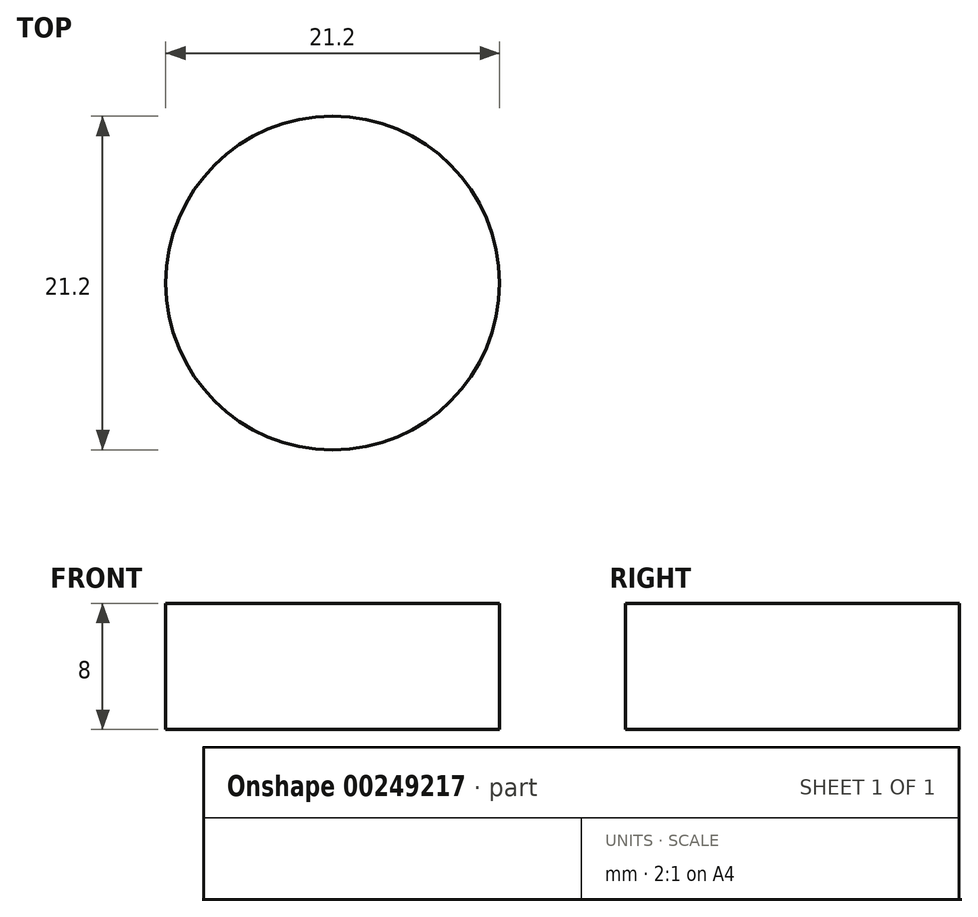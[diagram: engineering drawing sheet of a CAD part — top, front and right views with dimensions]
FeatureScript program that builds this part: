
annotation { "Feature Type Name" : "Feature", "Feature Type Description" : "" }
export const myFeature = defineFeature(function(context is Context, id is Id, definition is map)
    precondition{}
    {
        {
            var Q0;
            Q0=qCreatedBy(makeId("Top.planeOp"),FACE);
            var sketch = newSketch(context, id + "F0", { "sketchPlane" : qUnion([Q0])});
            skCircle(sketch, "E0", {"center": v(0, 0) * mm, "radius": 10.6 * mm});
            skSolve(sketch);
        }
        {
            var Q0;
            Q0 = qSketchRegion(id + "F0", true);
            extrude(context, id + "F1", {"entities" : qUnion([Q0]), "depth" : 8 * mm});
        }
    });
